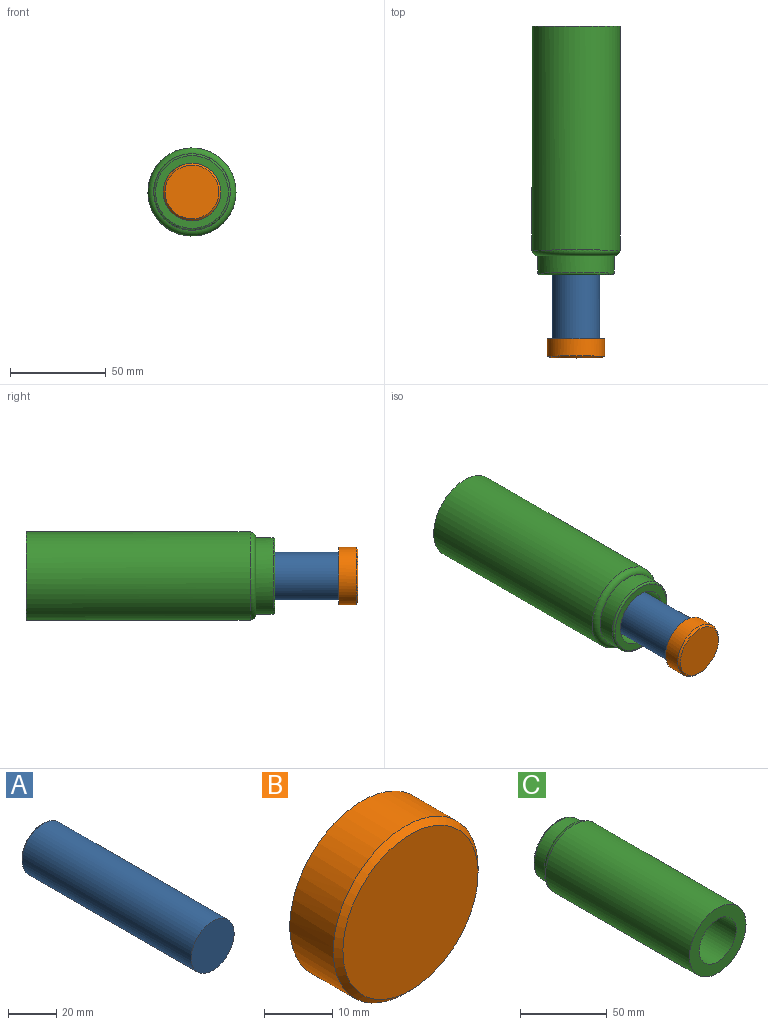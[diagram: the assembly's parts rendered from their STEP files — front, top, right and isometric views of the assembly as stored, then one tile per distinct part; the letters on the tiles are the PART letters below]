
ASSEMBLY  parts=3 mates=2
PART A: 4 faces, bbox 25x100x25 mm
  f0: cylinder r=12.5mm len=99mm, axis (0,-1,0), area 7775.4mm2, adj f2,f3
  f1: plane 23x23mm, normal (0,1,0), area 415.5mm2, adj f3
  f2: plane 25x25mm, normal (0,-1,0), area 490.9mm2, adj f0
  f3: cone r=11.5mm half-angle=45deg, axis (0,-1,0), area 106.6mm2, adj f0,f1
PART B: 6 faces, bbox 30x10x30 mm
  f0: cylinder r=15mm len=30mm, axis (0,1,0), area 848.2mm2, adj f2,f3
  f1: plane 28x28mm, normal (0,-1,0), area 615.8mm2, adj f3
  f2: plane 30x30mm, normal (0,1,0), area 216mm2, adj f0,f4
  f3: cone r=14mm half-angle=45deg, axis (0,1,0), area 128.8mm2, adj f0,f1
  f4: cylinder r=12.5mm len=25mm, axis (0,1,0), area 392.7mm2, adj f2,f5
  f5: plane 25x25mm, normal (0,1,0), area 490.9mm2, adj f4
PART C: 7 faces, bbox 49.8x130x49.8 mm
  f0: cylinder r=15mm len=130mm, axis (0,1,0), area 12252.2mm2, adj f2,f4
  f1: cylinder r=20mm len=40mm, axis (0,1,0), area 1131mm2, adj f5,f6
  f2: plane 38x38mm, normal (0,1,0), area 427.3mm2, adj f0,f6
  f3: cylinder r=23mm len=117mm, axis (0,1,0), area 16908.1mm2, adj f4,f5
  f4: plane 46x46mm, normal (0,-1,0), area 955mm2, adj f0,f3
  f5: torus R=20mm, axis (0,-1,0), area 648.7mm2, adj f1,f3
  f6: torus R=19mm, axis (0,-1,0), area 193.8mm2, adj f1,f2
PLACE A rot(axis=(0,1,0),90deg) t=(22.4,-58.68,14.82)mm
PLACE B rot(axis=(0,1,0),90deg) t=(22.4,-53.68,14.82)mm
PLACE C rot(axis=(1,0,0),180deg) t=(22.4,-10.33,14.82)mm fixed
MATE fastened B.f0 <-> A.f0  axis (0,1,0) through (22.4,-53.68,14.82)mm
MATE slider C.f0 <-> B.f0  axis (0,-1,0) through (22.4,-15.33,14.82)mm
